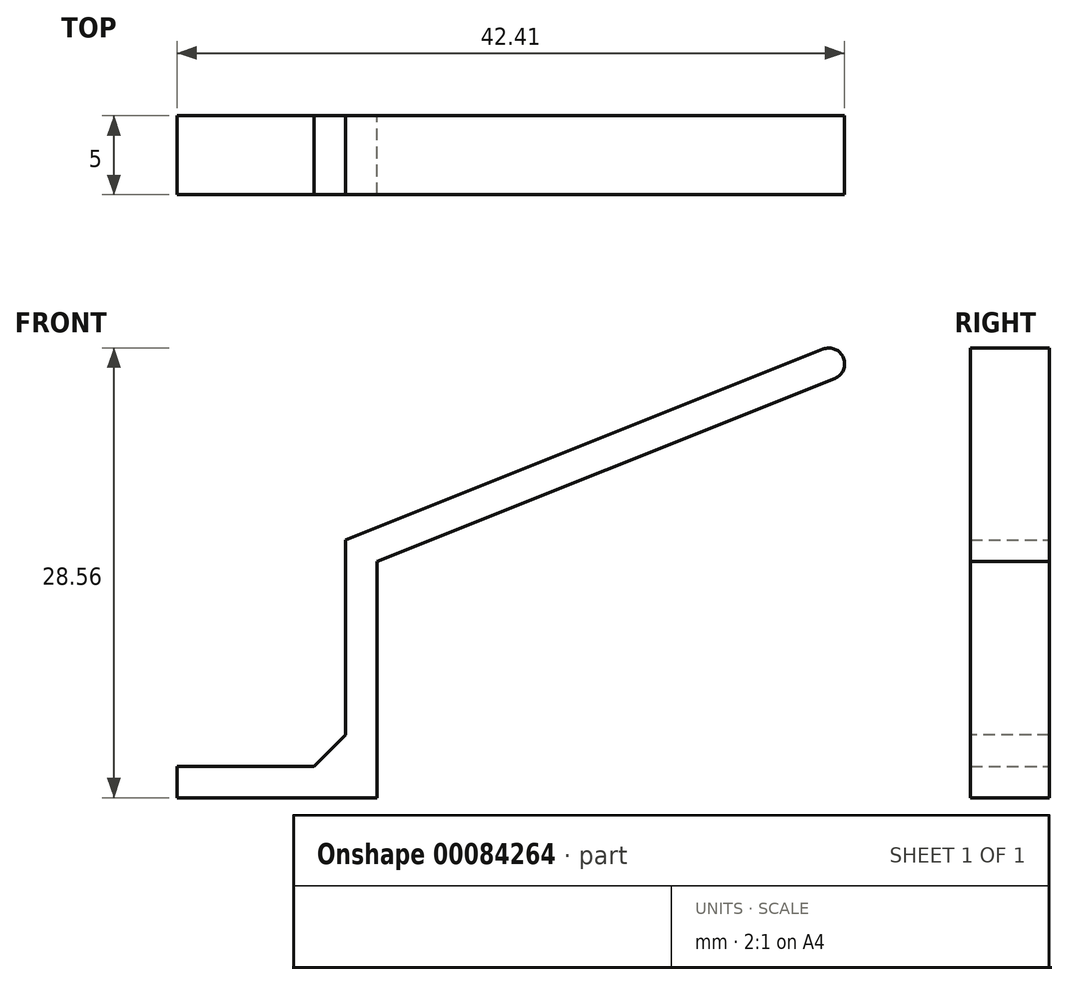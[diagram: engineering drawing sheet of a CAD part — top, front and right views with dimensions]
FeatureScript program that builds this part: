
annotation { "Feature Type Name" : "Feature", "Feature Type Description" : "" }
export const myFeature = defineFeature(function(context is Context, id is Id, definition is map)
    precondition{}
    {
        {
            var Q0;
            Q0=qCreatedBy(makeId("Front.planeOp"),FACE);
            var sketch = newSketch(context, id + "F0", { "sketchPlane" : qUnion([Q0])});
            skLineSegment(sketch, "E0", {"start": v(-10.75, 3.95) * mm, "end": v(-10.75, -11.05) * mm});
            skLineSegment(sketch, "E1", {"start": v(-10.75, -11.05) * mm, "end": v(19.25, -11.05) * mm});
            skLineSegment(sketch, "E2", {"start": v(19.25, -11.05) * mm, "end": v(19.25, 15.95) * mm});
            skLineSegment(sketch, "E3", {"start": v(19.25, 15.95) * mm, "end": v(-10.75, 3.95) * mm});
            skLineSegment(sketch, "E4", {"start": v(19.25, 15.95) * mm, "end": v(18.5, 17.8) * mm});
            skLineSegment(sketch, "E5", {"start": v(18.5, 17.8) * mm, "end": v(-12.75, 5.3) * mm});
            skLineSegment(sketch, "E6", {"start": v(-12.75, 5.3) * mm, "end": v(-12.75, -9.05) * mm});
            skLineSegment(sketch, "E7", {"start": v(-12.75, -9.05) * mm, "end": v(-23.46, -9.05) * mm});
            skLineSegment(sketch, "E8", {"start": v(-23.46, -9.05) * mm, "end": v(-23.46, -11.05) * mm});
            skLineSegment(sketch, "E9", {"start": v(-23.46, -11.05) * mm, "end": v(-10.75, -11.05) * mm});
            skSolve(sketch);
        }
        {
            var Q0;
            Q0=makeQuery(id+"F0.imprint","IMPRINT",FACE,{"disambiguationData":[TD([[makeQuery(id+"F0.imprint","IMPRINT",EDGE,{"derivedFrom":sQuery(id+"F0.wireOp",EDGE,"E0")}),-1.0]])]});
            extrude(context, id + "F1", {"entities" : qUnion([Q0]), "depth" : 5 * mm});
        }
        {
            var Q0;
            Q0=makeQuery(id+"F1.opExtrude","SWEPT_EDGE",EDGE,{"disambiguationData":[OSD([sQuery(id+"F0.wireOp",EDGE,"E6"),sQuery(id+"F0.wireOp",EDGE,"E7")])]});
            chamfer(context, id + "F2", {"entities" : qUnion([Q0]), "width" : 2 * mm, "tangentPropagation" : true});
        }
        {
            var Q0;
            Q0=makeQuery(id+"F1.opExtrude","SWEPT_EDGE",EDGE,{"disambiguationData":[OSD([sQuery(id+"F0.wireOp",EDGE,"E4"),sQuery(id+"F0.wireOp",EDGE,"E5")])]});
            var Q1;
            Q1=makeQuery(id+"F1.opExtrude","SWEPT_EDGE",EDGE,{"disambiguationData":[OSD([sQuery(id+"F0.wireOp",EDGE,"E2"),sQuery(id+"F0.wireOp",EDGE,"E3"),sQuery(id+"F0.wireOp",EDGE,"E4")])]});
            fillet(context, id + "F3", {"entities" : qUnion([Q0, Q1]), "radius" : 1 * mm, "tangentPropagation" : true, "allowEdgeOverflow" : false});
        }
    });
